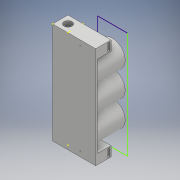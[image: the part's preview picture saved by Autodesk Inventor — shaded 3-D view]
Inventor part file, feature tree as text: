
AUTODESK INVENTOR PART (.ipt)
format: ipt  version: 2018 (Build 220112000, 112)  size: 289,280 bytes
history: native  units: mm
features: sketch x24, extrude x15, fillet x2
ambient origin geometry x8: Origin, YZ Plane, XZ Plane, XY Plane, X Axis, Y Axis, Z Axis, Center Point
bodies: Solid1 (feature_tree)
feature tree (41):
  extrude  "Extrusion1"  Depth=165.0mm
  extrude  "Extrusion2"  Depth=7.0mm
  sketch  "Sketch3"  dims[d5=7.0mm d6=22.0mm d7=0.0mm]
  extrude  "Extrusion3"  Depth=22.0mm TaperAngle=0.0deg
  extrude  "Extrusion4"  Depth=5.0mm TaperAngle=0.0deg
  extrude  "Extrusion5"  Depth=10.0mm
  sketch  "Sketch7"  dims[d18=7.5mm d19=0.0mm d20=2.0mm]
  sketch  "Sketch8"  dims[d21=3.0mm d22=45.0mm d23=0.0mm]
  extrude  "Extrusion6"  Depth=5.0mm
  fillet  "Fillet1"  Radius=5.0mm
  extrude  "Extrusion7"  Depth=2.0mm
  extrude  "Extrusion8"  Depth=45.0mm TaperAngle=0.0deg
  sketch  "Sketch12"  dims[d31=16.0mm d32=22.0mm d33=0.0mm]
  extrude  "Extrusion9"  Depth=38.65mm
  sketch  "Sketch14"  dims[d37=3.25mm d38=3.5mm d39=12.25mm]
  sketch  "Sketch15"  dims[d40=3.25mm d41=40.0mm d42=0.0mm]
  extrude  "Extrusion10"  Depth=38.65mm
  extrude  "Extrusion11"  Depth=16.0mm
  extrude  "Extrusion12"  Depth=22.0mm TaperAngle=0.0deg
  sketch  "Sketch17"  dims[d45=25.0mm]
  sketch  "Sketch18"  dims[d46=1.5mm]
  sketch  "Sketch19"  dims[d47=25.0mm d48=0.0mm]
  extrude  "Extrusion13"  Depth=12.25mm
  sketch  "Sketch21"  dims[d50=1.5mm]
  extrude  "Extrusion14"  Depth=3.5mm
  fillet  "Fillet2"  Radius=12.25mm
  extrude  "Extrusion15"  Depth=40.0mm TaperAngle=0.0deg
  sketch  "Sketch24"  dims[d54=1.0mm d55=5.25mm d56=0.0mm d57=1.0mm d58=1.0mm d59=5.25mm d60=0.0mm]
  sketch  "Sketch1"  dims[d0=25.0mm d1=165.0mm]
  sketch  "Sketch2"  dims[d2=3.0mm d3=0.0mm d4=7.0mm]
  sketch  "Sketch4"  dims[d8=13.0mm d9=5.0mm d10=0.0mm]
  sketch  "Sketch5"  dims[d11=5.0mm d12=0.0mm d13=10.0mm]
  sketch  "Sketch6"  dims[d14=165.0mm d15=0.0mm d16=5.0mm d17=5.0mm]
  sketch  "Sketch9"  dims[d24=42.0mm d25=38.65mm]
  sketch  "Sketch10"  dims[d26=38.65mm d27=38.65mm]
  sketch  "Sketch11"  dims[d28=45.0mm d29=0.0mm d30=16.0mm]
  sketch  "Sketch13"  dims[d35=3.5mm d36=12.25mm]
  sketch  "Sketch16"  dims[d43=40.0mm d44=0.0mm]
  sketch  "Sketch20"  dims[d49=25.0mm]
  sketch  "Sketch22"  dims[d51=25.0mm d52=0.0mm]
  sketch  "Sketch23"  dims[d53=2.0mm]
